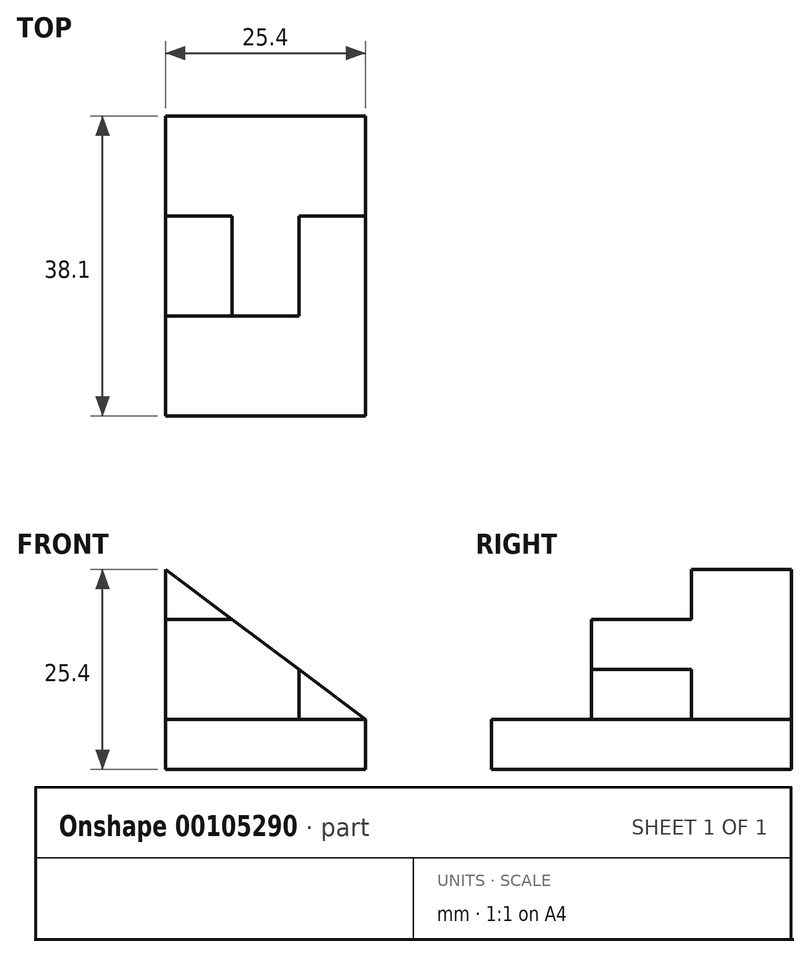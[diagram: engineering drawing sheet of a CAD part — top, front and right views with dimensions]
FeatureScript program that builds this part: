
annotation { "Feature Type Name" : "Feature", "Feature Type Description" : "" }
export const myFeature = defineFeature(function(context is Context, id is Id, definition is map)
    precondition{}
    {
        {
            var Q0;
            Q0=qCreatedBy(makeId("Front.planeOp"),FACE);
            var sketch = newSketch(context, id + "F0", { "sketchPlane" : qUnion([Q0])});
            skLineSegment(sketch, "E0", {"start": v(0, 0) * mm, "end": v(0, 6.35) * mm});
            skLineSegment(sketch, "E1", {"start": v(0, 6.35) * mm, "end": v(25.4, 6.35) * mm});
            skLineSegment(sketch, "E2", {"start": v(25.4, 6.35) * mm, "end": v(25.4, 0) * mm});
            skLineSegment(sketch, "E3", {"start": v(25.4, 0) * mm, "end": v(0, 0) * mm});
            skLineSegment(sketch, "E4", {"start": v(0, 6.35) * mm, "end": v(0, 19.05) * mm});
            skLineSegment(sketch, "E5", {"start": v(0, 19.05) * mm, "end": v(0, 25.4) * mm});
            skLineSegment(sketch, "E6", {"start": v(0, 25.4) * mm, "end": v(25.4, 6.35) * mm});
            skLineSegment(sketch, "E7", {"start": v(16.93, 12.7) * mm, "end": v(16.93, 6.35) * mm});
            skLineSegment(sketch, "E8", {"start": v(0, 19.05) * mm, "end": v(8.47, 19.05) * mm});
            skSolve(sketch);
        }
        {
            var Q0;
            {var subQ3=sQuery(id+"F0.wireOp",EDGE,"E0");Q0=makeQuery(id+"F0.imprint","IMPRINT",FACE,{"disambiguationData":[TD([[makeQuery(id+"F0.imprint","IMPRINT",EDGE,{"derivedFrom":subQ3}),-1.0]])]});}
            extrude(context, id + "F1", {"entities" : qUnion([Q0]), "depth" : 38.1 * mm});
        }
        {
            var Q0;
            {var subQ0=sQuery(id+"F0.wireOp",EDGE,"E5");Q0=makeQuery(id+"F0.imprint","IMPRINT",FACE,{"disambiguationData":[TD([[makeQuery(id+"F0.imprint","IMPRINT",EDGE,{"derivedFrom":subQ0}),-1.0]])]});}
            extrude(context, id + "F2", {"entities" : qUnion([Q0]), "depth" : 12.7 * mm});
        }
        {
            var Q0;
            {var subQ3=sQuery(id+"F0.wireOp",EDGE,"E4");Q0=makeQuery(id+"F0.imprint","IMPRINT",FACE,{"disambiguationData":[TD([[makeQuery(id+"F0.imprint","IMPRINT",EDGE,{"derivedFrom":subQ3}),-1.0]])]});}
            extrude(context, id + "F3", {"entities" : qUnion([Q0]), "operationType" : NewBodyOperationType.ADD, "depth" : 25.4 * mm});
        }
        {
            var Q0;
            {var subQ3=sQuery(id+"F0.wireOp",EDGE,"E7");Q0=makeQuery(id+"F0.imprint","IMPRINT",FACE,{"disambiguationData":[TD([[makeQuery(id+"F0.imprint","IMPRINT",EDGE,{"derivedFrom":subQ3}),1.0]])]});}
            extrude(context, id + "F4", {"entities" : qUnion([Q0]), "operationType" : NewBodyOperationType.ADD, "depth" : 12.7 * mm});
        }
    });
